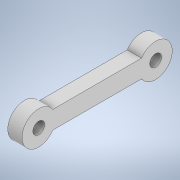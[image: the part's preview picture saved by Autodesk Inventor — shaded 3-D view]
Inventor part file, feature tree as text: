
AUTODESK INVENTOR PART (.ipt)
format: ipt  version: 2020 (Build 240168000, 168)  size: 116,736 bytes
history: native  units: in
note: dims shown in document units (in); Inventor stores cm internally (conversion verified against a paired STEP export)
features: extrude x1, sketch x1
ambient origin geometry x8: Origin, YZ Plane, XZ Plane, XY Plane, X Axis, Y Axis, Z Axis, Center Point
bodies: Solid1 (feature_tree)
feature tree (2):
  extrude  "Extrusion1"  Depth=1.2852in
  sketch  "Sketch1"  dims[d0=0.1299in d1=1.2852in d2=0.1181in d3=0.1181in d4=0.1969in d5=0.1575in d6=0.0in]
